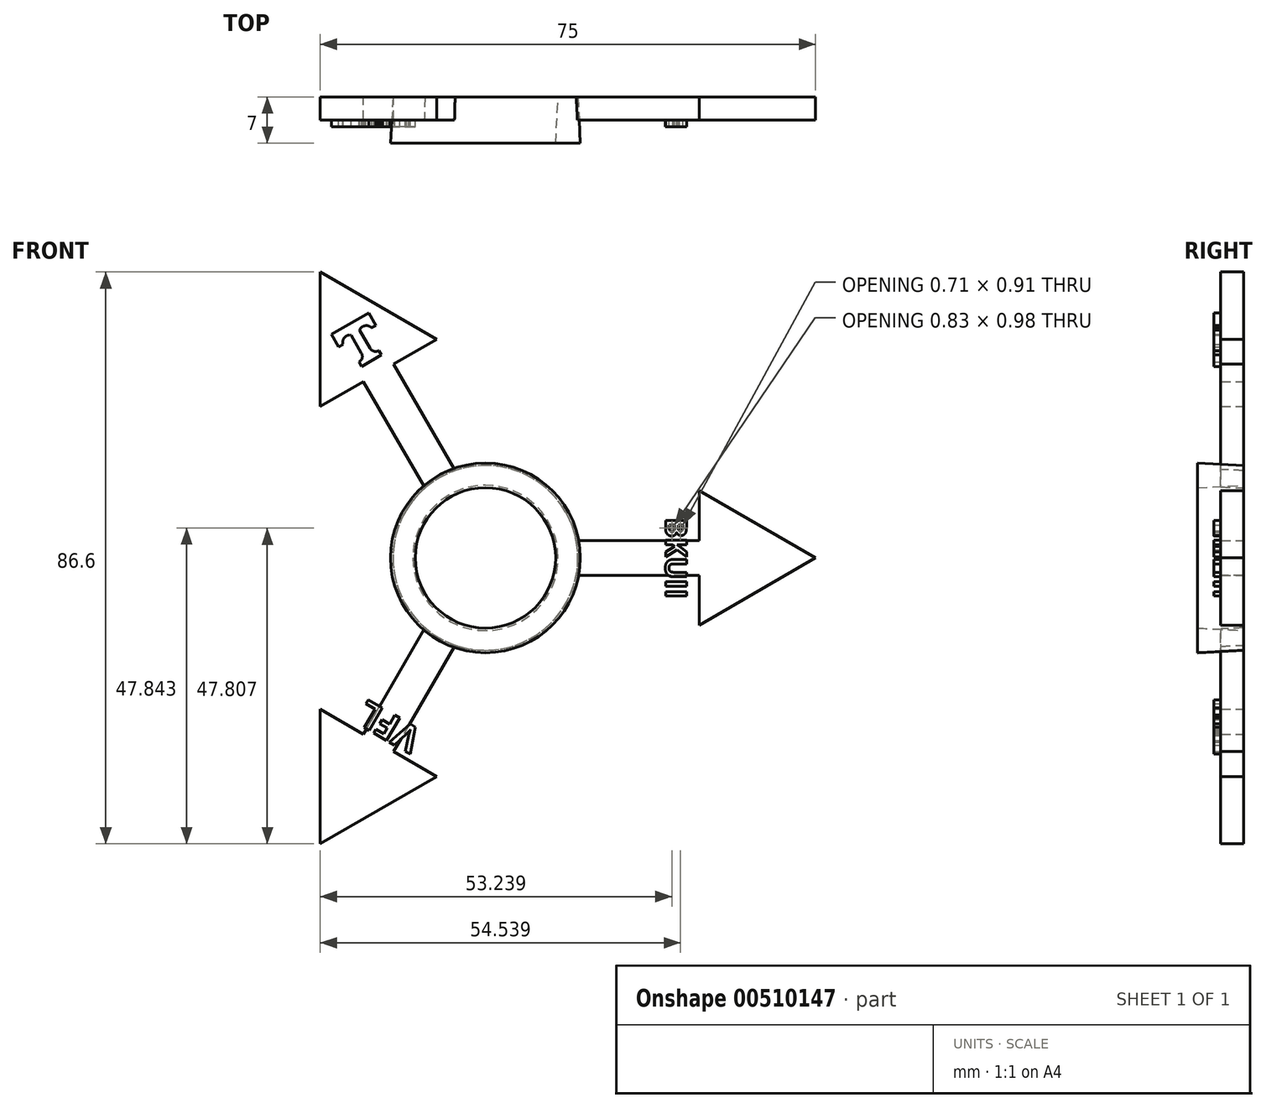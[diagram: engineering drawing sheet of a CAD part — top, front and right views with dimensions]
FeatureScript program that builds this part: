
annotation { "Feature Type Name" : "Feature", "Feature Type Description" : "" }
export const myFeature = defineFeature(function(context is Context, id is Id, definition is map)
    precondition{}
    {
        {
            var Q0;
            Q0=qCreatedBy(makeId("Front.planeOp"),FACE);
            var sketch = newSketch(context, id + "F0", { "sketchPlane" : qUnion([Q0])});
            skCircle(sketch, "E0", {"center": v(0, 0) * mm, "radius": 11 * mm});
            skCircle(sketch, "E1", {"center": v(0, 0) * mm, "radius": 14 * mm});
            skSolve(sketch);
        }
        {
            var Q0;
            Q0=makeQuery(id+"F0.imprint","IMPRINT",FACE,{"disambiguationData":[TD([[makeQuery(id+"F0.imprint","IMPRINT",EDGE,{"derivedFrom":sQuery(id+"F0.wireOp",EDGE,"E0")}),-1.0]])]});
            extrude(context, id + "F1", {"entities" : qUnion([Q0]), "depth" : 7 * mm, "hasDraft" : true, "draftAngle" : 3 * degree});
        }
        {
            var Q0;
            Q0=qCreatedBy(makeId("Front.planeOp"),FACE);
            var sketch = newSketch(context, id + "F2", { "sketchPlane" : qUnion([Q0])});
            skCircle(sketch, "E2.cCircle", {"center": v(38.24, 0) * mm, "radius": 5.88 * mm, "construction": true});
            skLineSegment(sketch, "E2.0", {"start": v(50, 0) * mm, "end": v(32.36, -10.19) * mm});
            skLineSegment(sketch, "E2.1", {"start": v(32.36, -10.19) * mm, "end": v(32.36, 10.19) * mm});
            skLineSegment(sketch, "E2.2", {"start": v(32.36, 10.19) * mm, "end": v(50, 0) * mm});
            skPoint(sketch, "E2.0.midPoint", {"position": v(41.18, -5.1) * mm});
            skCircle(sketch, "E3", {"center": v(0, 0) * mm, "radius": 14 * mm});
            skLineSegment(sketch, "E4", {"start": v(13.75, 2.64) * mm, "end": v(32.36, 2.64) * mm});
            skLineSegment(sketch, "E5", {"start": v(32.36, -2.64) * mm, "end": v(13.75, -2.64) * mm});
            skSolve(sketch);
        }
        {
            var Q0;
            {var subQ0=sQuery(id+"F2.wireOp",EDGE,"E4");Q0=makeQuery(id+"F2.imprint","IMPRINT",FACE,{"disambiguationData":[TD([[makeQuery(id+"F2.imprint","IMPRINT",EDGE,{"derivedFrom":subQ0}),-1.0]])]});}
            var Q1;
            {var subQ4=sQuery(id+"F2.wireOp",EDGE,"E2.0");Q1=makeQuery(id+"F2.imprint","IMPRINT",FACE,{"disambiguationData":[TD([[makeQuery(id+"F2.imprint","IMPRINT",EDGE,{"derivedFrom":subQ4}),-1.0]])]});}
            extrude(context, id + "F3", {"entities" : qUnion([Q0, Q1]), "operationType" : NewBodyOperationType.ADD, "depth" : 3.5 * mm});
        }
        {
            var Q0;
            Q0=makeQuery(id+"F1.opExtrude","SWEPT_BODY",BODY,{"disambiguationData":[OSD([sQuery(id+"F0.wireOp",EDGE,"E0"),sQuery(id+"F0.wireOp",EDGE,"E1")])]});
            var Q1;
            Q1=makeQuery(id+"F1.opExtrude","CAP_EDGE",EDGE,{"disambiguationData":[OSD([sQuery(id+"F0.wireOp",EDGE,"E0")])],"isStart":false});
            circularPattern(context, id + "F4", {"entities" : qUnion([Q0]), "axis" : qUnion([Q1]), "angle" : 360 * degree, "instanceCount" : 3, "equalSpace" : true});
        }
        {
            var Q0;
            Q0=makeQuery(id+"F4.opPattern","COPY",FACE,{"derivedFrom":makeQuery(id+"F3.opExtrude","CAP_FACE",FACE,{"disambiguationData":[OSD([sQuery(id+"F2.wireOp",EDGE,"E2.0"),sQuery(id+"F2.wireOp",EDGE,"E2.1"),sQuery(id+"F2.wireOp",EDGE,"E2.2"),sQuery(id+"F2.wireOp",EDGE,"E3"),sQuery(id+"F2.wireOp",EDGE,"E4"),sQuery(id+"F2.wireOp",EDGE,"E5")])],"isStart":false}),"instanceName":"1"});
            var sketch = newSketch(context, id + "F5", { "sketchPlane" : qUnion([Q0])});
            skLineSegment(sketch, "E6", {"start": v(0, 0) * mm, "end": v(-25, 43.3) * mm});
            skLineSegment(sketch, "E7", {"start": v(0, 0) * mm, "end": v(-25, -43.3) * mm});
            skPoint(sketch, "E8.0", {"position": v(-25, -43.3) * mm});
            skLineSegment(sketch, "E9", {"start": v(0, 0) * mm, "end": v(50, 0) * mm});
            skPoint(sketch, "E10.0", {"position": v(50, 0) * mm});
            skText(sketch, "E11", { "text": "BKUII", "fontName": "OpenSans-Bold.ttf"});
            skLineSegment(sketch, "E12", {"start": v(-20.5, 35.5) * mm, "end": v(-17.69, 37.13) * mm});
            skLineSegment(sketch, "E13", {"start": v(-17.69, 37.13) * mm, "end": v(-16.59, 35.23) * mm});
            skLineSegment(sketch, "E14", {"start": v(-16.59, 35.23) * mm, "end": v(-17.23, 34.85) * mm});
            skLineSegment(sketch, "E15", {"start": v(-20.5, 35.5) * mm, "end": v(-17.25, 29.88) * mm, "construction": true});
            skLineSegment(sketch, "E16", {"start": v(-17.25, 29.88) * mm, "end": v(-15.73, 30.75) * mm});
            skLineSegment(sketch, "E17", {"start": v(-15.73, 30.75) * mm, "end": v(-16.1, 31.4) * mm});
            skLineSegment(sketch, "E18", {"start": v(-19.06, 34.5) * mm, "end": v(-17.48, 31.77) * mm});
            skArc(sketch, "E19", {"start": v(-17.48, 31.77) * mm, "mid": v(-16.87, 31.3) * mm, "end": v(-16.1, 31.4) * mm});
            skLineSegment(sketch, "E20", {"start": v(-16.1, 31.4) * mm, "end": v(-12.85, 33.28) * mm, "construction": true});
            skArc(sketch, "E21", {"start": v(-17.23, 34.85) * mm, "mid": v(-18.24, 35.16) * mm, "end": v(-19.06, 34.5) * mm});
            skLineSegment(sketch, "E22.MirrorCS", {"start": v(-19.14, 29.65) * mm, "end": v(-22.4, 27.77) * mm, "construction": true});
            skLineSegment(sketch, "E23.MirrorCS", {"start": v(-22.21, 31.98) * mm, "end": v(-21.57, 32.35) * mm});
            skLineSegment(sketch, "E24.MirrorCS", {"start": v(-17.25, 29.88) * mm, "end": v(-18.77, 29) * mm});
            skLineSegment(sketch, "E25.MirrorCS", {"start": v(-18.77, 29) * mm, "end": v(-19.14, 29.65) * mm});
            skLineSegment(sketch, "E26.MirrorCS", {"start": v(-20.36, 33.76) * mm, "end": v(-18.77, 31.02) * mm});
            skLineSegment(sketch, "E27.MirrorCS", {"start": v(-23.31, 33.88) * mm, "end": v(-22.21, 31.98) * mm});
            skLineSegment(sketch, "E28.MirrorCS", {"start": v(-20.5, 35.5) * mm, "end": v(-23.31, 33.88) * mm});
            skArc(sketch, "E29.MirrorCS", {"start": v(-18.77, 31.02) * mm, "mid": v(-18.67, 30.26) * mm, "end": v(-19.14, 29.65) * mm});
            skArc(sketch, "E30.MirrorCS", {"start": v(-21.57, 32.35) * mm, "mid": v(-21.33, 33.37) * mm, "end": v(-20.36, 33.76) * mm});
            skText(sketch, "E31", { "text": "VFL", "fontName": "OpenSans-Bold.ttf"});
            const initialGuessF5  = {"E11": [0.02727, 0.00607, 0, -1, 0.0032], "E31": [-0.00942, -0.02629, -0.86603, 0.5, 0.004]};
            skSetInitialGuess(sketch, initialGuessF5);
            skSolve(sketch);
        }
        {
            var Q0;
            Q0 = qSketchRegion(id + "F5", true);
            extrude(context, id + "F6", {"entities" : qUnion([Q0]), "depth" : 1 * mm});
        }
    });
